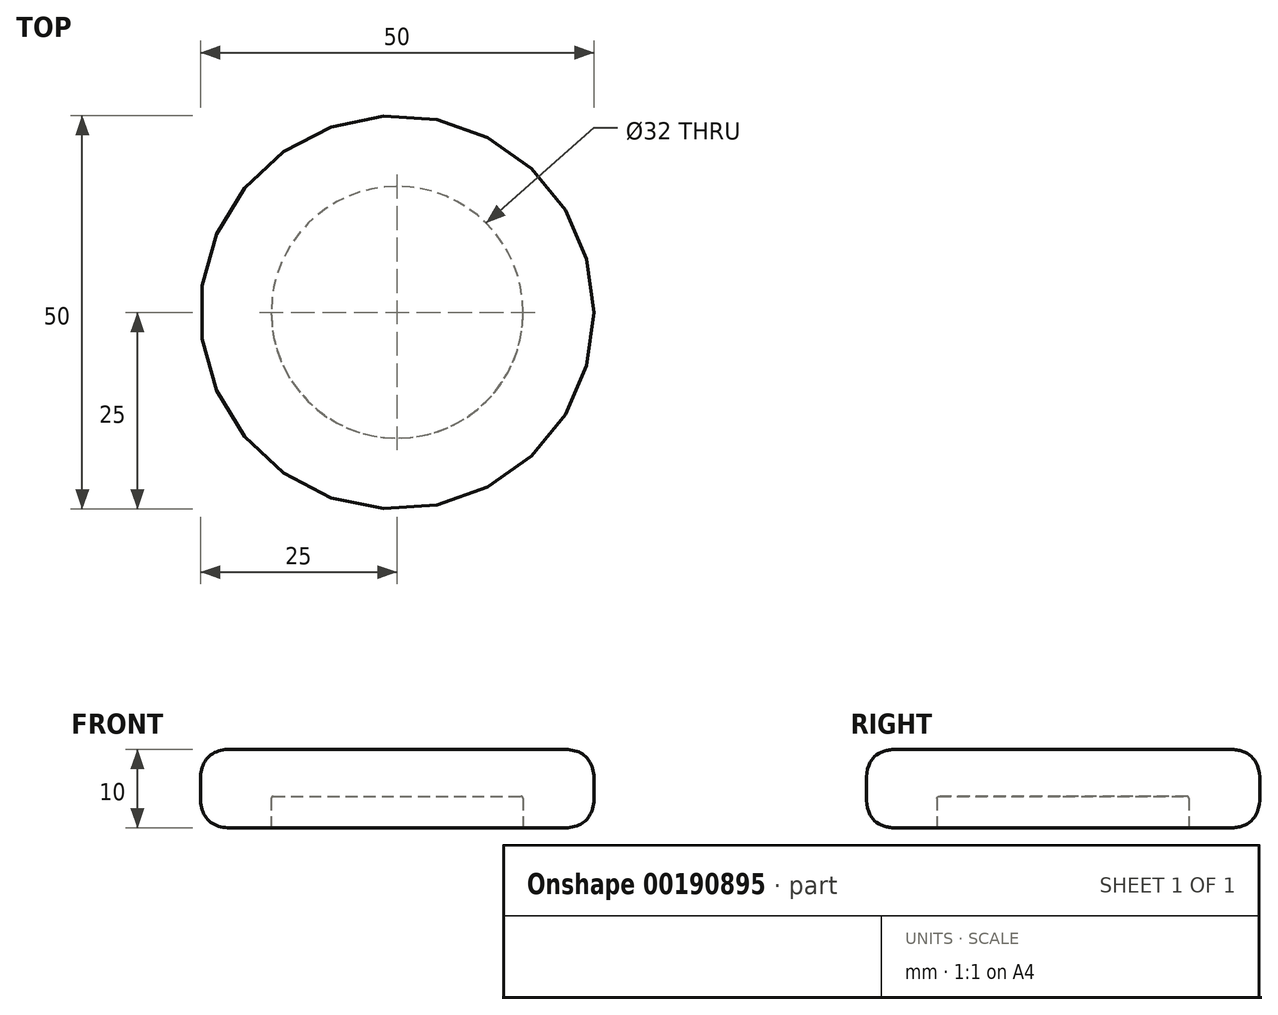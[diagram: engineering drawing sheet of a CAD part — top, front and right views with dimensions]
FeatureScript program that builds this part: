
annotation { "Feature Type Name" : "Feature", "Feature Type Description" : "" }
export const myFeature = defineFeature(function(context is Context, id is Id, definition is map)
    precondition{}
    {
        {
            var Q0;
            Q0=qCreatedBy(makeId("Top.planeOp"),FACE);
            var sketch = newSketch(context, id + "F0", { "sketchPlane" : qUnion([Q0])});
            skCircle(sketch, "E0", {"center": v(0, 0) * mm, "radius": 25 * mm});
            skSolve(sketch);
        }
        {
            var Q0;
            Q0 = qSketchRegion(id + "F0", true);
            extrude(context, id + "F1", {"entities" : qUnion([Q0]), "depth" : 10 * mm, "offsetDistance" : 25 * mm, "symmetric" : true});
        }
        {
            var Q0;
            Q0=makeQuery(id+"F1.opExtrude","SWEPT_FACE",FACE,{"disambiguationData":[OSD([sQuery(id+"F0.wireOp",EDGE,"E0")])]});
            fillet(context, id + "F2", {"entities" : qUnion([Q0]), "radius" : 4 * mm, "tangentPropagation" : true, "rho" : 0.5, "crossSection" : FilletCrossSection.CONIC, "allowEdgeOverflow" : false});
        }
        {
            var Q0;
            Q0=makeQuery(id+"F1.opExtrude","CAP_FACE",FACE,{"disambiguationData":[OSD([sQuery(id+"F0.wireOp",EDGE,"E0")])],"isStart":true});
            var sketch = newSketch(context, id + "F3", { "sketchPlane" : qUnion([Q0])});
            skCircle(sketch, "E1", {"center": v(0, 0) * mm, "radius": 16 * mm});
            skSolve(sketch);
        }
        {
            var Q0;
            Q0 = qSketchRegion(id + "F3", true);
            extrude(context, id + "F4", {"entities" : qUnion([Q0]), "operationType" : NewBodyOperationType.REMOVE, "oppositeDirection" : true, "depth" : 4 * mm, "offsetDistance" : 25 * mm});
        }
        {
            var Q0;
            Q0=makeQuery(id+"F4.boolean.opBoolean","COPY",FACE,{"derivedFrom":makeQuery(id+"F4.opExtrude","SWEPT_FACE",FACE,{"disambiguationData":[OSD([sQuery(id+"F3.wireOp",EDGE,"E1")])]})});
            fillet(context, id + "F5", {"entities" : qUnion([Q0]), "radius" : 0.25 * mm, "tangentPropagation" : true, "allowEdgeOverflow" : false});
        }
    });
